# Revit family: Plum Fix_Toilet Pan_Children's_Argent_Pace HygienicFlush_S-Trap
name_source: partatom
category: Plumbing Fixtures
revit_build: Autodesk Revit 2016 (Build: 20190508_0715(x64)
units: mm (PartAtom-declared; Revit-internal decimal feet)

## family parameters
Always vertical = Yes
Cut with Voids When Loaded = Yes
OmniClass Number = 23.45.05.21.11
OmniClass Title = Water Closets
Part Type = Normal
Room Calculation Point = No
Round Connector Dimension = Use Diameter
Shared = No
Work Plane-Based = No

## types (1)
- White (WC1001S)
    BodyMaterial = z_Argent_Ceramic White
    CW Connection = Yes
    CWFU = 0
    Cost = 0 $
    Description = Pace HygienicFlush Children's Toilet
    HW Connection = No
    HWFU = 0
    IfcExportAs = IfcSanitaryTerminalType
    IfcExportType = TOILETPAN
    Manufacturer = Argent
    Manufacturer_Overall Depth = 550 mm
    Manufacturer_Overall Height = 610 mm  [stored 2.00131 ft]
    Manufacturer_Overall Width = 255 mm  [stored 0.836614 ft]
    Manufacturer_Spec Code = WC1001S
    Manufacturer_URL__Product Specific = https://www.argentaust.com.au
    Model = WC1001S
    ModifiedIssue_ANZRS = 20191126 $
    Toilet P Trap = Yes
    Toilet S Trap = Yes
    Type Comments = S-Trap
    URL = https://www.argentaust.com.au
    Uniclass2015Code = Pr_40_20_93_97
    Uniclass2015Title = WC suites
    Uniclass2015Version = Products v1.5
    Vent Connection = No
    WFU = 0
    Waste Connection = Yes

note: [stored X ft] marks values corroborated as IEEE doubles in the binary element streams (Revit-internal decimal feet)

## geometry (parser evidence)
native form markers: Sweep x1
no freeform markers — native parametric forms only
